# Revit family: Digidim Router (Two Dali Subnets)_910
name_source: partatom
category: Electrical Fixtures
revit_build: Autodesk Revit 2018 (Build: 20170223_1515(x64)
units: mm (PartAtom-declared; Revit-internal decimal feet)

## family parameters
Always vertical = Yes
Cut with Voids When Loaded = No
Maintain Annotation Orientation = No
OmniClass Number = 23.80.00.00
OmniClass Title = Electric Power and Lighting
Part Type = Normal
Room Calculation Point = No
Round Connector Dimension = Use Diameter
Shared = No
Work Plane-Based = Yes

## types (1)
- Digidim Router (Two Dali Subnets)
    Ambient temperature = 0 °C to + 40 °C
    DALI cable = 2-wire mains rated,
0.5 mm² – 2.5 mm²
Max. length: 300 m @ 1.5 mm²
    DALI data transfer = DALI-2 Application Controller
(Single Master) parts 101, 103
    DALI-OUT current: = 2×240 mA (guaranteed) 2x250mA (maximum)
    Default Elevation = 0 mm  [stored 0 ft]
    Dimensions: = 9U – 160 mm × 100 mm × 58 mm
    EMC emission = EN 55022 Class A
    EMC immunity = EN 55024
    Environment = Complies with WEEE and RoHS directives.
    Ethernet = 1 × RJ45 10/100 Mb/s, Cat 5E
up to 100 m (Auto MDI/MDI-X
crossover)
    IP code: = IP30 (IP00 at connectors)
    Mains Cable = Solid core up to 4 mm²
Stranded up to 2.5 mm²
    Mains Supply = 100 VAC – 240 VAC (nominal)
85 VAC – 264 VAC (absolute)
45 Hz – 65 Hz
    Manufacturer = Helvar
    Model = 910
    Mounting = DIN Rail. Keep mains and DALI
wiring separate from Ethernet cable
    Power Circuit Protection = External protection max. 6 A.
Earth mandatory.
    Power consumption = 23 VA (DALI subnet fully loaded)
    Relative humidity = Max. 90 %, noncondensing
    Safety = EN 60950
    Storage temperature = −10 °C to + 70 °C
    Weight: = 260 g

note: [stored X ft] marks values corroborated as IEEE doubles in the binary element streams (Revit-internal decimal feet)

## geometry (parser evidence)
native form markers: Sweep x1
no freeform markers — native parametric forms only
